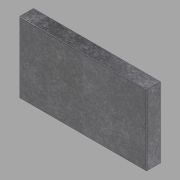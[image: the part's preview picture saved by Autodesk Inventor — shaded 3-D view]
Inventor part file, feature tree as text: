
AUTODESK INVENTOR PART (.ipt)
format: ipt  version: 2022.1 (Build 261234020, 234B)  size: 115,200 bytes
history: native  units: in
note: dims shown in document units (in); Inventor stores cm internally (conversion verified against a paired STEP export)
features: extrude x1, fillet x1, sketch x1
ambient origin geometry x8: Origin, YZ Plane, XZ Plane, XY Plane, X Axis, Y Axis, Z Axis, Center Point
bodies: Solid1 (feature_tree)
feature tree (3):
  extrude  "Extrusion1"  Depth=30.0in
  fillet  "Fillet1"  Radius=6.0in
  sketch  "Sketch1"  dims[d0=54.0in d1=30.0in d2=6.0in d3=0.0in d4=0.25in]
